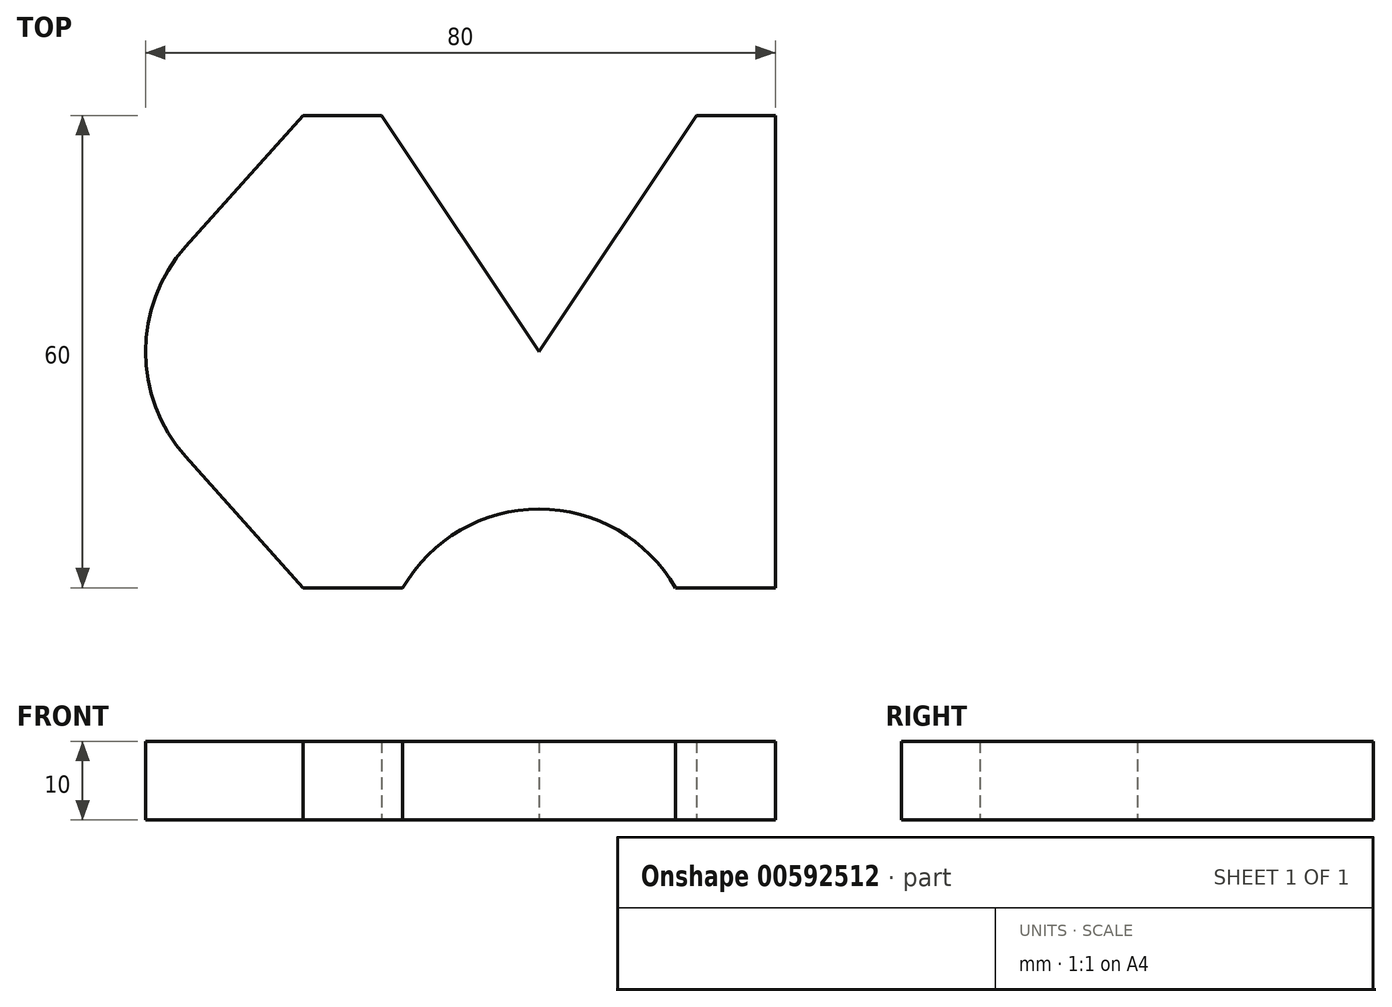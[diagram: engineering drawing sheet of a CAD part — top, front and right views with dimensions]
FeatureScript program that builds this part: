
annotation { "Feature Type Name" : "Feature", "Feature Type Description" : "" }
export const myFeature = defineFeature(function(context is Context, id is Id, definition is map)
    precondition{}
    {
        {
            var Q0;
            Q0=qCreatedBy(makeId("Top.planeOp"),FACE);
            var sketch = newSketch(context, id + "F0", { "sketchPlane" : qUnion([Q0])});
            skLineSegment(sketch, "E0", {"start": v(20, 30) * mm, "end": v(30, 30) * mm});
            skLineSegment(sketch, "E1", {"start": v(30, 30) * mm, "end": v(30, -30) * mm});
            skLineSegment(sketch, "E2", {"start": v(30, -30) * mm, "end": v(17.32, -30) * mm});
            skArc(sketch, "E3", {"start": v(17.32, -30) * mm, "mid": v(0, -20) * mm, "end": v(-17.32, -30) * mm});
            skLineSegment(sketch, "E4", {"start": v(-17.32, -30) * mm, "end": v(-30, -30) * mm});
            skLineSegment(sketch, "E5", {"start": v(-30, 30) * mm, "end": v(-20, 30) * mm});
            skLineSegment(sketch, "E6", {"start": v(-20, 30) * mm, "end": v(0, 0) * mm});
            skLineSegment(sketch, "E7", {"start": v(0, 0) * mm, "end": v(20, 30) * mm});
            skLineSegment(sketch, "E8", {"start": v(-30, -30) * mm, "end": v(-44.9, -13.33) * mm});
            skArc(sketch, "E9", {"start": v(-44.9, 13.33) * mm, "mid": v(-50, 0) * mm, "end": v(-44.9, -13.33) * mm});
            skLineSegment(sketch, "E10", {"start": v(-44.9, 13.33) * mm, "end": v(-30, 30) * mm});
            skLineSegment(sketch, "E11", {"start": v(-30, 30) * mm, "end": v(-30, -30) * mm, "construction": true});
            skLineSegment(sketch, "E12", {"start": v(0, 0) * mm, "end": v(30, 0) * mm, "construction": true});
            skSolve(sketch);
        }
        {
            var Q0;
            Q0=makeQuery(id+"F0.imprint","IMPRINT",FACE,{"disambiguationData":[TD([[makeQuery(id+"F0.imprint","IMPRINT",EDGE,{"derivedFrom":sQuery(id+"F0.wireOp",EDGE,"E0")}),-1.0]])]});
            extrude(context, id + "F1", {"entities" : qUnion([Q0]), "depth" : 10 * mm, "offsetDistance" : 25 * mm});
        }
    });
